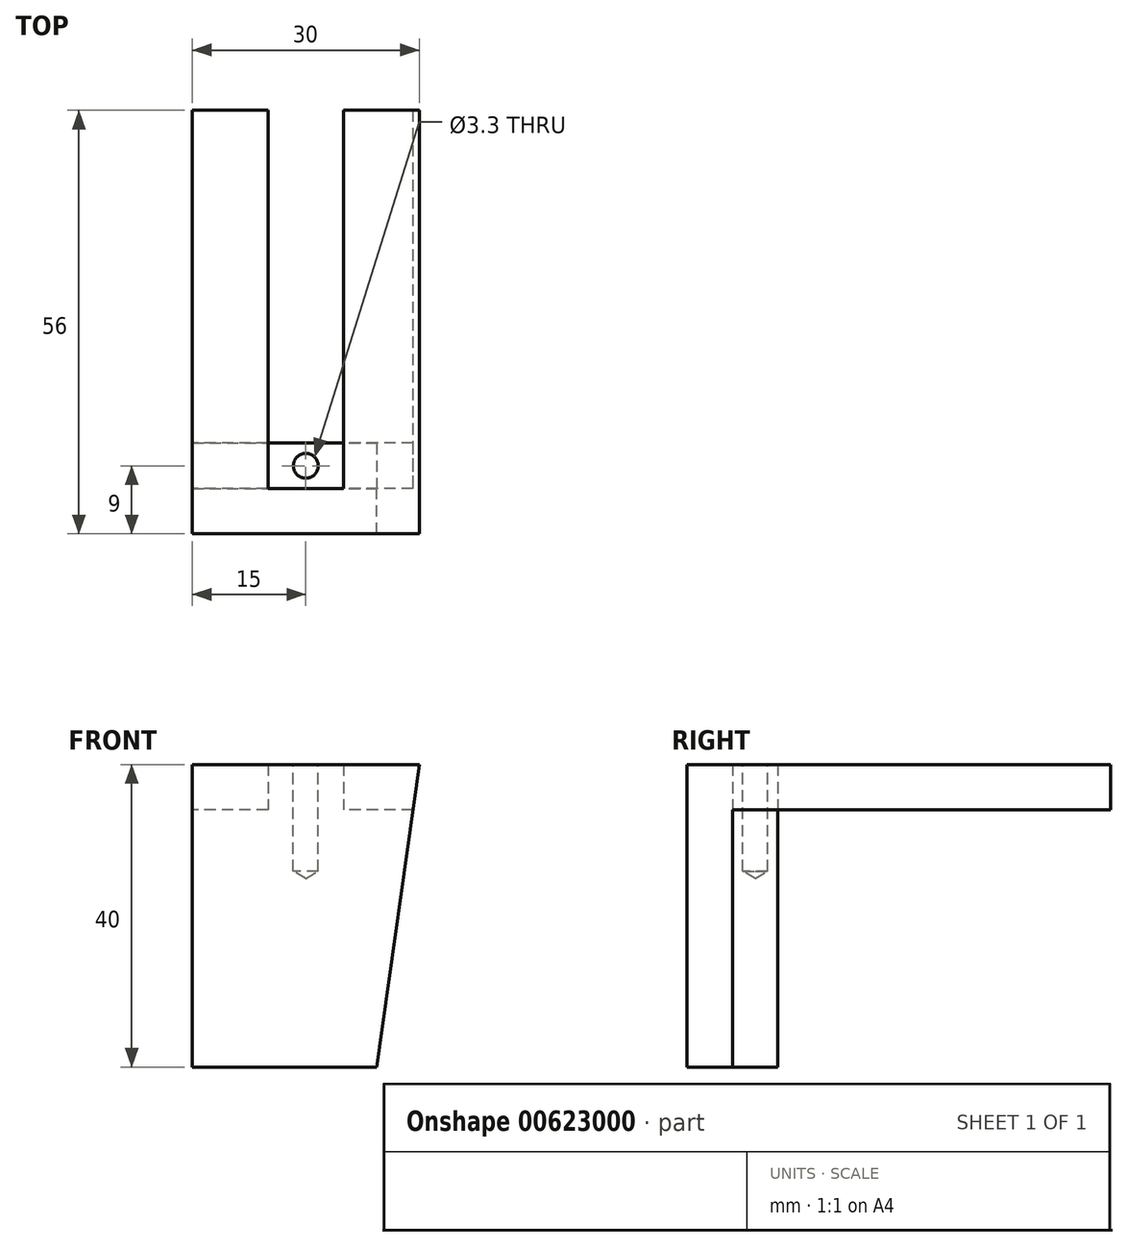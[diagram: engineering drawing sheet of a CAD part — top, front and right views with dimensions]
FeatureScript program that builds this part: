
annotation { "Feature Type Name" : "Feature", "Feature Type Description" : "" }
export const myFeature = defineFeature(function(context is Context, id is Id, definition is map)
    precondition{}
    {
        {
            var Q0;
            Q0=qCreatedBy(makeId("Front.planeOp"),FACE);
            var sketch = newSketch(context, id + "F0", { "sketchPlane" : qUnion([Q0])});
            skPoint(sketch, "E0.middle", {"position": v(0, 0) * mm});
            skLineSegment(sketch, "E1", {"start": v(-15, -32.5) * mm, "end": v(9.38, -32.5) * mm});
            skLineSegment(sketch, "E2", {"start": v(9.38, -32.5) * mm, "end": v(9.38, -7.5) * mm, "construction": true});
            skLineSegment(sketch, "E3", {"start": v(15, 7.5) * mm, "end": v(9.38, -32.5) * mm});
            skLineSegment(sketch, "E4", {"start": v(-15, 7.5) * mm, "end": v(-15, -32.5) * mm});
            skLineSegment(sketch, "E5", {"start": v(-15, 7.5) * mm, "end": v(15, 7.5) * mm});
            skLineSegment(sketch, "E6", {"start": v(-15, 1.5) * mm, "end": v(14.16, 1.5) * mm, "construction": true});
            skSolve(sketch);
        }
        {
            var Q0;
            Q0 = qSketchRegion(id + "F0", true);
            extrude(context, id + "F1", {"entities" : qUnion([Q0]), "depth" : 6 * mm, "offsetDistance" : 25 * mm});
        }
        {
            var Q0;
            Q0=makeQuery(id+"F1.opExtrude","CAP_FACE",FACE,{"disambiguationData":[OSD([sQuery(id+"F0.wireOp",EDGE,"E1"),sQuery(id+"F0.wireOp",EDGE,"E3"),sQuery(id+"F0.wireOp",EDGE,"E4"),sQuery(id+"F0.wireOp",EDGE,"E5")])],"isStart":true});
            var sketch = newSketch(context, id + "F2", { "sketchPlane" : qUnion([Q0])});
            skLineSegment(sketch, "E7.0", {"start": v(15, 7.5) * mm, "end": v(-15, 7.5) * mm});
            skPoint(sketch, "E8.orphan", {"position": v(-9.38, -32.5) * mm});
            skPoint(sketch, "E9.orphan", {"position": v(15, -32.5) * mm});
            skLineSegment(sketch, "E10", {"start": v(-14.16, 1.5) * mm, "end": v(15, 1.5) * mm});
            skLineSegment(sketch, "E11.bottom", {"start": v(-5, 7.5) * mm, "end": v(5, 7.5) * mm});
            skLineSegment(sketch, "E11.top", {"start": v(-5, 1.5) * mm, "end": v(5, 1.5) * mm});
            skLineSegment(sketch, "E11.left", {"start": v(-5, 7.5) * mm, "end": v(-5, 1.5) * mm});
            skLineSegment(sketch, "E11.right", {"start": v(5, 7.5) * mm, "end": v(5, 1.5) * mm});
            skLineSegment(sketch, "E12", {"start": v(-15, 7.5) * mm, "end": v(-14.16, 1.5) * mm});
            skLineSegment(sketch, "E13", {"start": v(15, 7.5) * mm, "end": v(15, 1.5) * mm});
            skSolve(sketch);
        }
        {
            var Q0;
            {var subQ3=sQuery(id+"F2.wireOp",EDGE,"E11.right");Q0=makeQuery(id+"F2.imprint","IMPRINT",FACE,{"disambiguationData":[TD([[makeQuery(id+"F2.imprint","IMPRINT",EDGE,{"derivedFrom":subQ3}),1.0]])]});}
            var Q1;
            {var subQ3=sQuery(id+"F2.wireOp",EDGE,"E11.left");Q1=makeQuery(id+"F2.imprint","IMPRINT",FACE,{"disambiguationData":[TD([[makeQuery(id+"F2.imprint","IMPRINT",EDGE,{"derivedFrom":subQ3}),-1.0]])]});}
            extrude(context, id + "F3", {"entities" : qUnion([Q0, Q1]), "operationType" : NewBodyOperationType.ADD, "depth" : 50 * mm, "offsetDistance" : 25 * mm});
        }
        {
            var Q0;
            Q0=makeQuery(id+"F1.opExtrude","CAP_FACE",FACE,{"disambiguationData":[OSD([sQuery(id+"F0.wireOp",EDGE,"E1"),sQuery(id+"F0.wireOp",EDGE,"E3"),sQuery(id+"F0.wireOp",EDGE,"E4"),sQuery(id+"F0.wireOp",EDGE,"E5")])],"isStart":true});
            extrude(context, id + "F4", {"entities" : qUnion([Q0]), "depth" : 6 * mm, "offsetDistance" : 25 * mm});
        }
        {
            var Q0;
            Q0=makeQuery(id+"F4.opExtrude","SWEPT_FACE",FACE,{"disambiguationData":[OSD([sQuery(id+"F0.wireOp",EDGE,"E5")])]});
            var sketch = newSketch(context, id + "F5", { "sketchPlane" : qUnion([Q0])});
            skPoint(sketch, "E14", {"position": v(0, 3) * mm});
            skPoint(sketch, "E14.positionSnap0", {"position": v(-5, 3) * mm});
            skSolve(sketch);
        }
        {
            var Q0;
            Q0=sQuery(id+"F5.wireOp",VERTEX,"E14");
            var Q1;
            Q1=makeQuery(id+"F4.opExtrude","SWEPT_BODY",BODY,{"disambiguationData":[OSD([sQuery(id+"F0.wireOp",EDGE,"E1"),sQuery(id+"F0.wireOp",EDGE,"E3"),sQuery(id+"F0.wireOp",EDGE,"E4"),sQuery(id+"F0.wireOp",EDGE,"E5")])]});
            hole(context, id + "F6", {"style" : HoleStyle.SIMPLE, "endStyle" : HoleEndStyle.BLIND, "standardTappedOrClearance" : lookupTablePath({ "standard" : "ISO", "engagement" : "75%", "pitch" : "0.7 mm", "size" : "M4", "type" : "Tapped" }), "standardBlindInLast" : lookupTablePath({ "standard" : "ISO", "engagement" : "75%", "pitch" : "0.7 mm", "size" : "M4", "type" : "Tapped" }), "holeDiameter" : 3.3 * mm, "majorDiameter" : 4 * mm, "showTappedDepth" : true, "holeDepth" : 14.1 * mm, "isTappedThrough" : true, "tappedDepth" : 12 * mm, "tapClearance" : 3, "locations" : qUnion([Q0]), "scope" : qUnion([Q1])});
        }
    });
